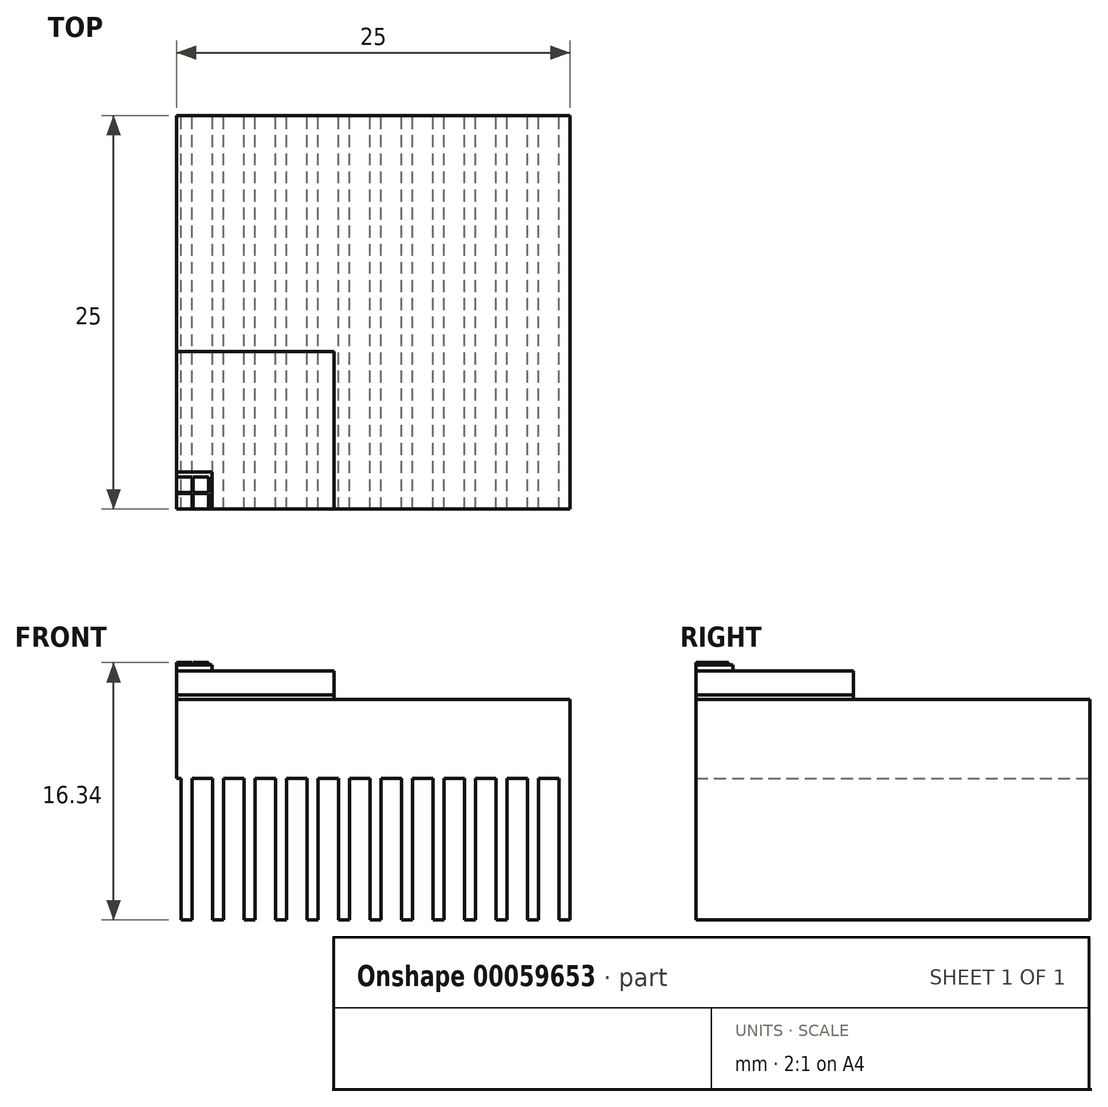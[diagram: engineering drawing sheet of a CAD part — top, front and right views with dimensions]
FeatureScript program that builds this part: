
annotation { "Feature Type Name" : "Feature", "Feature Type Description" : "" }
export const myFeature = defineFeature(function(context is Context, id is Id, definition is map)
    precondition{}
    {
        {
            var Q0;
            Q0=qCreatedBy(makeId("Top.planeOp"),FACE);
            var sketch = newSketch(context, id + "F0", { "sketchPlane" : qUnion([Q0])});
            skLineSegment(sketch, "E0.bottom", {"start": v(0, 0) * mm, "end": v(10, 0) * mm});
            skLineSegment(sketch, "E0.top", {"start": v(0, 10) * mm, "end": v(10, 10) * mm});
            skLineSegment(sketch, "E0.left", {"start": v(0, 0) * mm, "end": v(0, 10) * mm});
            skLineSegment(sketch, "E0.right", {"start": v(10, 0) * mm, "end": v(10, 10) * mm});
            skSolve(sketch);
        }
        {
            var Q0;
            Q0 = qSketchRegion(id + "F0", true);
            extrude(context, id + "F1", {"entities" : qUnion([Q0]), "depth" : 1.5 * mm});
        }
        {
            var Q0;
            Q0=makeQuery(id+"F1.opExtrude","CAP_FACE",FACE,{"disambiguationData":[OSD([sQuery(id+"F0.wireOp",EDGE,"E0.bottom"),sQuery(id+"F0.wireOp",EDGE,"E0.top"),sQuery(id+"F0.wireOp",EDGE,"E0.left"),sQuery(id+"F0.wireOp",EDGE,"E0.right")])],"isStart":false});
            var sketch = newSketch(context, id + "F2", { "sketchPlane" : qUnion([Q0])});
            skLineSegment(sketch, "E1.bottom", {"start": v(0, 0) * mm, "end": v(2.24, 0) * mm});
            skLineSegment(sketch, "E1.top", {"start": v(0, 2.35) * mm, "end": v(2.24, 2.35) * mm});
            skLineSegment(sketch, "E1.left", {"start": v(0, 0) * mm, "end": v(0, 2.35) * mm});
            skLineSegment(sketch, "E1.right", {"start": v(2.24, 0) * mm, "end": v(2.24, 2.35) * mm});
            skSolve(sketch);
        }
        {
            var Q0;
            Q0 = qSketchRegion(id + "F2", true);
            extrude(context, id + "F3", {"entities" : qUnion([Q0]), "depth" : .4 * mm});
        }
        {
            var Q0;
            Q0=makeQuery(id+"F3.opExtrude","CAP_FACE",FACE,{"disambiguationData":[OSD([sQuery(id+"F2.wireOp",EDGE,"E1.bottom"),sQuery(id+"F2.wireOp",EDGE,"E1.top"),sQuery(id+"F2.wireOp",EDGE,"E1.left"),sQuery(id+"F2.wireOp",EDGE,"E1.right")])],"isStart":false});
            var sketch = newSketch(context, id + "F4", { "sketchPlane" : qUnion([Q0])});
            skLineSegment(sketch, "E2.bottom", {"start": v(0, 0) * mm, "end": v(1, 0) * mm});
            skLineSegment(sketch, "E2.top", {"start": v(0, 1) * mm, "end": v(1, 1) * mm});
            skLineSegment(sketch, "E2.left", {"start": v(0, 0) * mm, "end": v(0, 1) * mm});
            skLineSegment(sketch, "E2.right", {"start": v(1, 0) * mm, "end": v(1, 1) * mm});
            skLineSegment(sketch, "E3.bottom", {"start": v(0, 2.05) * mm, "end": v(1, 2.05) * mm});
            skLineSegment(sketch, "E3.top", {"start": v(0, 1.05) * mm, "end": v(1, 1.05) * mm});
            skLineSegment(sketch, "E3.left", {"start": v(0, 2.05) * mm, "end": v(0, 1.05) * mm});
            skLineSegment(sketch, "E3.right", {"start": v(1, 2.05) * mm, "end": v(1, 1.05) * mm});
            skLineSegment(sketch, "E4.bottom", {"start": v(1.05, 2.05) * mm, "end": v(2.05, 2.05) * mm});
            skLineSegment(sketch, "E4.top", {"start": v(1.05, 1.05) * mm, "end": v(2.05, 1.05) * mm});
            skLineSegment(sketch, "E4.left", {"start": v(1.05, 2.05) * mm, "end": v(1.05, 1.05) * mm});
            skLineSegment(sketch, "E4.right", {"start": v(2.05, 2.05) * mm, "end": v(2.05, 1.05) * mm});
            skLineSegment(sketch, "E5.bottom", {"start": v(1.05, 1) * mm, "end": v(2.05, 1) * mm});
            skLineSegment(sketch, "E5.top", {"start": v(1.05, 0) * mm, "end": v(2.05, 0) * mm});
            skLineSegment(sketch, "E5.left", {"start": v(1.05, 1) * mm, "end": v(1.05, 0) * mm});
            skLineSegment(sketch, "E5.right", {"start": v(2.05, 1) * mm, "end": v(2.05, 0) * mm});
            skSolve(sketch);
        }
        {
            var Q0;
            Q0 = qSketchRegion(id + "F4", true);
            extrude(context, id + "F5", {"entities" : qUnion([Q0]), "depth" : .145 * mm});
        }
        {
            var Q0;
            Q0=makeQuery(id+"F1.opExtrude","CAP_FACE",FACE,{"disambiguationData":[OSD([sQuery(id+"F0.wireOp",EDGE,"E0.bottom"),sQuery(id+"F0.wireOp",EDGE,"E0.top"),sQuery(id+"F0.wireOp",EDGE,"E0.left"),sQuery(id+"F0.wireOp",EDGE,"E0.right")])],"isStart":true});
            var sketch = newSketch(context, id + "F6", { "sketchPlane" : qUnion([Q0])});
            skLineSegment(sketch, "E6.bottom", {"start": v(10, 0) * mm, "end": v(0, 0) * mm});
            skLineSegment(sketch, "E6.top", {"start": v(10, -10) * mm, "end": v(0, -10) * mm});
            skLineSegment(sketch, "E6.left", {"start": v(10, 0) * mm, "end": v(10, -10) * mm});
            skLineSegment(sketch, "E6.right", {"start": v(0, 0) * mm, "end": v(0, -10) * mm});
            skSolve(sketch);
        }
        {
            var Q0;
            Q0 = qSketchRegion(id + "F6", true);
            extrude(context, id + "F7", {"entities" : qUnion([Q0]), "depth" : .3 * mm});
        }
        {
            var Q0;
            Q0=makeQuery(id+"F7.opExtrude","CAP_FACE",FACE,{"disambiguationData":[OSD([sQuery(id+"F6.wireOp",EDGE,"E6.bottom"),sQuery(id+"F6.wireOp",EDGE,"E6.top"),sQuery(id+"F6.wireOp",EDGE,"E6.left"),sQuery(id+"F6.wireOp",EDGE,"E6.right")])],"isStart":false});
            var sketch = newSketch(context, id + "F8", { "sketchPlane" : qUnion([Q0])});
            skLineSegment(sketch, "E7.bottom", {"start": v(0, 0) * mm, "end": v(25, 0) * mm});
            skLineSegment(sketch, "E7.top", {"start": v(0, -25) * mm, "end": v(25, -25) * mm});
            skLineSegment(sketch, "E7.left", {"start": v(0, 0) * mm, "end": v(0, -25) * mm});
            skLineSegment(sketch, "E7.right", {"start": v(25, 0) * mm, "end": v(25, -25) * mm});
            skSolve(sketch);
        }
        {
            var Q0;
            Q0 = qSketchRegion(id + "F8", true);
            extrude(context, id + "F9", {"entities" : qUnion([Q0]), "depth" : 5 * mm});
        }
        {
            var Q0;
            Q0=makeQuery(id+"F9.opExtrude","CAP_FACE",FACE,{"disambiguationData":[OSD([sQuery(id+"F8.wireOp",EDGE,"E7.bottom"),sQuery(id+"F8.wireOp",EDGE,"E7.top"),sQuery(id+"F8.wireOp",EDGE,"E7.left"),sQuery(id+"F8.wireOp",EDGE,"E7.right")])],"isStart":false});
            var sketch = newSketch(context, id + "F10", { "sketchPlane" : qUnion([Q0])});
            skLineSegment(sketch, "E8.bottom", {"start": v(25, 0) * mm, "end": v(24.3, 0) * mm});
            skLineSegment(sketch, "E8.top", {"start": v(25, -25) * mm, "end": v(24.3, -25) * mm});
            skLineSegment(sketch, "E8.left", {"start": v(25, 0) * mm, "end": v(25, -25) * mm});
            skLineSegment(sketch, "E8.right", {"start": v(24.3, 0) * mm, "end": v(24.3, -25) * mm});
            skLineSegment(sketch, "E9.1.0.0", {"start": v(23, 0) * mm, "end": v(23, -25) * mm});
            skLineSegment(sketch, "E9.1.0.1", {"start": v(23, 0) * mm, "end": v(22.3, 0) * mm});
            skLineSegment(sketch, "E9.1.0.2", {"start": v(22.3, 0) * mm, "end": v(22.3, -25) * mm});
            skLineSegment(sketch, "E9.1.0.3", {"start": v(23, -25) * mm, "end": v(22.3, -25) * mm});
            skLineSegment(sketch, "E9.2.0.0", {"start": v(21, 0) * mm, "end": v(21, -25) * mm});
            skLineSegment(sketch, "E9.2.0.1", {"start": v(21, 0) * mm, "end": v(20.3, 0) * mm});
            skLineSegment(sketch, "E9.2.0.2", {"start": v(20.3, 0) * mm, "end": v(20.3, -25) * mm});
            skLineSegment(sketch, "E9.2.0.3", {"start": v(21, -25) * mm, "end": v(20.3, -25) * mm});
            skLineSegment(sketch, "E9.3.0.0", {"start": v(19, 0) * mm, "end": v(19, -25) * mm});
            skLineSegment(sketch, "E9.3.0.1", {"start": v(19, 0) * mm, "end": v(18.3, 0) * mm});
            skLineSegment(sketch, "E9.3.0.2", {"start": v(18.3, 0) * mm, "end": v(18.3, -25) * mm});
            skLineSegment(sketch, "E9.3.0.3", {"start": v(19, -25) * mm, "end": v(18.3, -25) * mm});
            skLineSegment(sketch, "E9.4.0.0", {"start": v(17, 0) * mm, "end": v(17, -25) * mm});
            skLineSegment(sketch, "E9.4.0.1", {"start": v(17, 0) * mm, "end": v(16.3, 0) * mm});
            skLineSegment(sketch, "E9.4.0.2", {"start": v(16.3, 0) * mm, "end": v(16.3, -25) * mm});
            skLineSegment(sketch, "E9.4.0.3", {"start": v(17, -25) * mm, "end": v(16.3, -25) * mm});
            skLineSegment(sketch, "E9.5.0.0", {"start": v(15, 0) * mm, "end": v(15, -25) * mm});
            skLineSegment(sketch, "E9.5.0.1", {"start": v(15, 0) * mm, "end": v(14.3, 0) * mm});
            skLineSegment(sketch, "E9.5.0.2", {"start": v(14.3, 0) * mm, "end": v(14.3, -25) * mm});
            skLineSegment(sketch, "E9.5.0.3", {"start": v(15, -25) * mm, "end": v(14.3, -25) * mm});
            skLineSegment(sketch, "E9.6.0.0", {"start": v(13, 0) * mm, "end": v(13, -25) * mm});
            skLineSegment(sketch, "E9.6.0.1", {"start": v(13, 0) * mm, "end": v(12.3, 0) * mm});
            skLineSegment(sketch, "E9.6.0.2", {"start": v(12.3, 0) * mm, "end": v(12.3, -25) * mm});
            skLineSegment(sketch, "E9.6.0.3", {"start": v(13, -25) * mm, "end": v(12.3, -25) * mm});
            skLineSegment(sketch, "E9.7.0.0", {"start": v(11, 0) * mm, "end": v(11, -25) * mm});
            skLineSegment(sketch, "E9.7.0.1", {"start": v(11, 0) * mm, "end": v(10.3, 0) * mm});
            skLineSegment(sketch, "E9.7.0.2", {"start": v(10.3, 0) * mm, "end": v(10.3, -25) * mm});
            skLineSegment(sketch, "E9.7.0.3", {"start": v(11, -25) * mm, "end": v(10.3, -25) * mm});
            skLineSegment(sketch, "E9.8.0.0", {"start": v(9, 0) * mm, "end": v(9, -25) * mm});
            skLineSegment(sketch, "E9.8.0.1", {"start": v(9, 0) * mm, "end": v(8.3, 0) * mm});
            skLineSegment(sketch, "E9.8.0.2", {"start": v(8.3, 0) * mm, "end": v(8.3, -25) * mm});
            skLineSegment(sketch, "E9.8.0.3", {"start": v(9, -25) * mm, "end": v(8.3, -25) * mm});
            skLineSegment(sketch, "E9.9.0.0", {"start": v(7, 0) * mm, "end": v(7, -25) * mm});
            skLineSegment(sketch, "E9.9.0.1", {"start": v(7, 0) * mm, "end": v(6.3, 0) * mm});
            skLineSegment(sketch, "E9.9.0.2", {"start": v(6.3, 0) * mm, "end": v(6.3, -25) * mm});
            skLineSegment(sketch, "E9.9.0.3", {"start": v(7, -25) * mm, "end": v(6.3, -25) * mm});
            skLineSegment(sketch, "E9.10.0.0", {"start": v(5, 0) * mm, "end": v(5, -25) * mm});
            skLineSegment(sketch, "E9.10.0.1", {"start": v(5, 0) * mm, "end": v(4.3, 0) * mm});
            skLineSegment(sketch, "E9.10.0.2", {"start": v(4.3, 0) * mm, "end": v(4.3, -25) * mm});
            skLineSegment(sketch, "E9.10.0.3", {"start": v(5, -25) * mm, "end": v(4.3, -25) * mm});
            skLineSegment(sketch, "E9.11.0.0", {"start": v(3, 0) * mm, "end": v(3, -25) * mm});
            skLineSegment(sketch, "E9.11.0.1", {"start": v(3, 0) * mm, "end": v(2.3, 0) * mm});
            skLineSegment(sketch, "E9.11.0.2", {"start": v(2.3, 0) * mm, "end": v(2.3, -25) * mm});
            skLineSegment(sketch, "E9.11.0.3", {"start": v(3, -25) * mm, "end": v(2.3, -25) * mm});
            skLineSegment(sketch, "E9.12.0.0", {"start": v(1, 0) * mm, "end": v(1, -25) * mm});
            skLineSegment(sketch, "E9.12.0.1", {"start": v(1, 0) * mm, "end": v(0.3, 0) * mm});
            skLineSegment(sketch, "E9.12.0.2", {"start": v(0.3, 0) * mm, "end": v(0.3, -25) * mm});
            skLineSegment(sketch, "E9.12.0.3", {"start": v(1, -25) * mm, "end": v(0.3, -25) * mm});
            skLineSegment(sketch, "E9.direction1", {"start": v(25, -25) * mm, "end": v(23, -25) * mm, "construction": true});
            skSolve(sketch);
        }
        {
            var Q0;
            Q0 = qSketchRegion(id + "F10", true);
            extrude(context, id + "F11", {"entities" : qUnion([Q0]), "operationType" : NewBodyOperationType.ADD, "depth" : 9 * mm});
        }
    });
